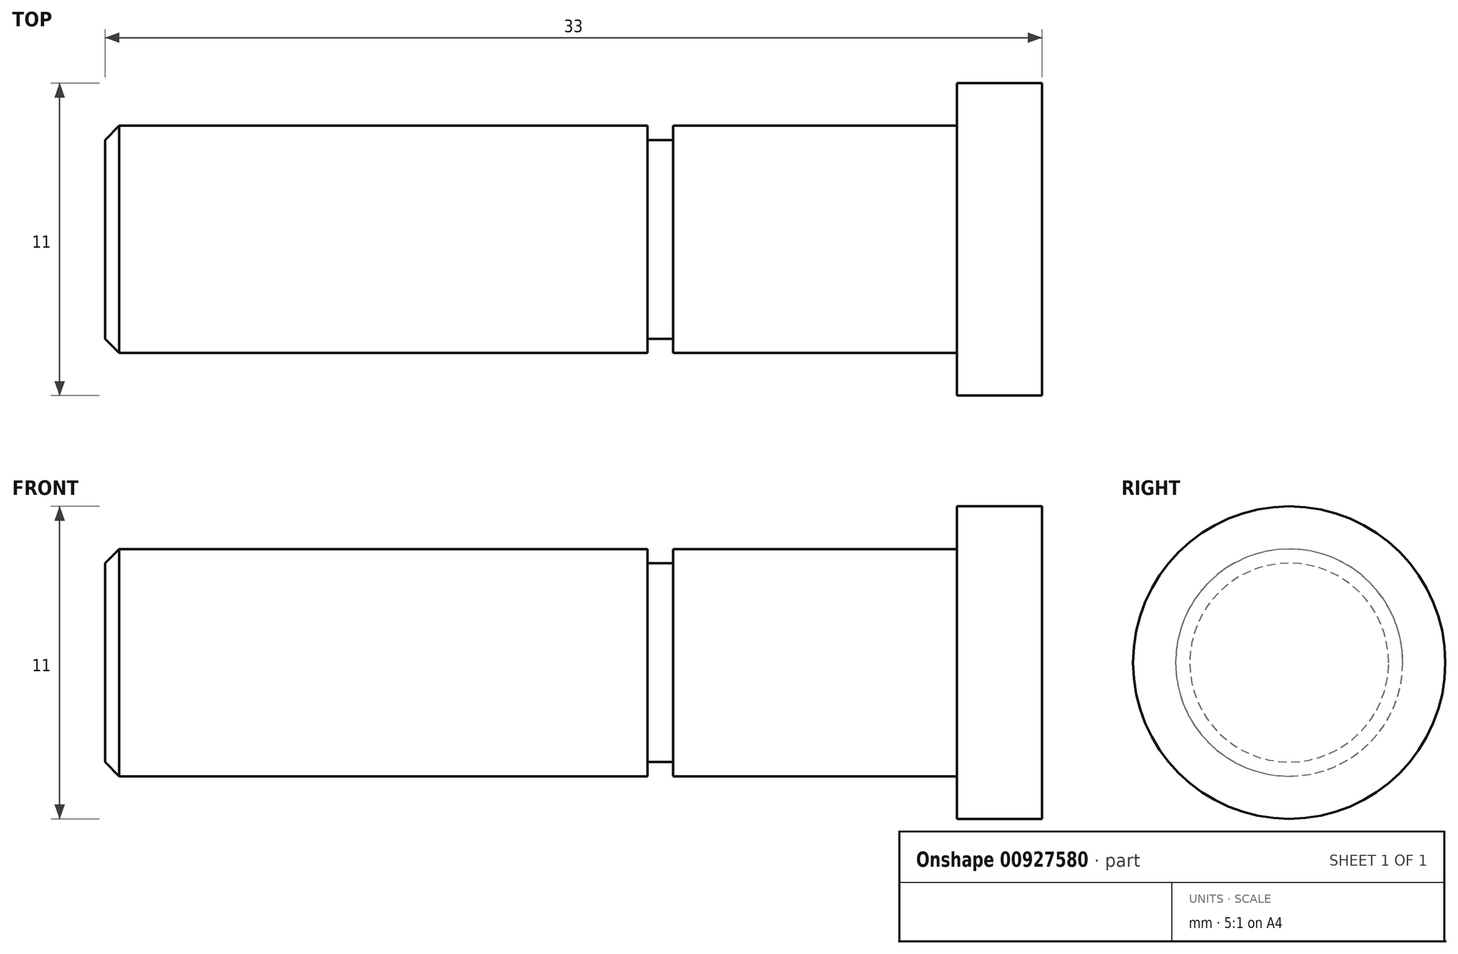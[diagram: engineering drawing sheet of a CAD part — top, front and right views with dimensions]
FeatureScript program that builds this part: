
annotation { "Feature Type Name" : "Feature", "Feature Type Description" : "" }
export const myFeature = defineFeature(function(context is Context, id is Id, definition is map)
    precondition{}
    {
        {
            var Q0;
            Q0=qCreatedBy(makeId("Right.planeOp"),FACE);
            var sketch = newSketch(context, id + "F0", { "sketchPlane" : qUnion([Q0])});
            skCircle(sketch, "E0", {"center": v(0, 0) * mm, "radius": 5.5 * mm});
            skSolve(sketch);
        }
        {
            var Q0;
            Q0 = qSketchRegion(id + "F0", true);
            extrude(context, id + "F1", {"entities" : qUnion([Q0]), "oppositeDirection" : true, "depth" : 3 * mm, "offsetDistance" : 25 * mm});
        }
        {
            var Q0;
            Q0=makeQuery(id+"F1.opExtrude","CAP_FACE",FACE,{"disambiguationData":[OSD([sQuery(id+"F0.wireOp",EDGE,"E0")])],"isStart":false});
            var sketch = newSketch(context, id + "F2", { "sketchPlane" : qUnion([Q0])});
            skCircle(sketch, "E1", {"center": v(0, 0) * mm, "radius": 4 * mm});
            skSolve(sketch);
        }
        {
            var Q0;
            Q0 = qSketchRegion(id + "F2", true);
            extrude(context, id + "F3", {"entities" : qUnion([Q0]), "operationType" : NewBodyOperationType.ADD, "depth" : 30 * mm, "offsetDistance" : 25 * mm});
        }
        {
            var Q0;
            Q0=qCreatedBy(makeId("Front.planeOp"),FACE);
            var sketch = newSketch(context, id + "F4", { "sketchPlane" : qUnion([Q0])});
            skLineSegment(sketch, "E2", {"start": v(-13, 15.33) * mm, "end": v(-13, -6.2) * mm, "construction": true});
            skLineSegment(sketch, "E3", {"start": v(-13, 4) * mm, "end": v(-13, 3.5) * mm});
            skLineSegment(sketch, "E4", {"start": v(-13, 3.5) * mm, "end": v(-13.9, 3.5) * mm});
            skLineSegment(sketch, "E5", {"start": v(-13.9, 3.5) * mm, "end": v(-13.9, 4) * mm});
            skLineSegment(sketch, "E6", {"start": v(-38, 0) * mm, "end": v(5.54, 0) * mm, "construction": true});
            skLineSegment(sketch, "E7", {"start": v(-13.9, 4) * mm, "end": v(-13, 4) * mm});
            skSolve(sketch);
        }
        {
            var Q0;
            Q0 = qSketchRegion(id + "F4", true);
            var Q1;
            Q1=sQuery(id+"F4.wireOp",EDGE,"E6");
            revolve(context, id + "F5", {"operationType" : NewBodyOperationType.REMOVE, "surfaceOperationType" : NewSurfaceOperationType.NEW, "entities" : qUnion([Q0]), "axis" : qUnion([Q1]), "revolveType" : RevolveType.FULL, "oppositeDirection" : true});
        }
        {
            var Q0;
            Q0=makeQuery(id+"F3.opExtrude","CAP_EDGE",EDGE,{"disambiguationData":[OSD([sQuery(id+"F2.wireOp",EDGE,"E1")])],"isStart":false});
            chamfer(context, id + "F6", {"entities" : qUnion([Q0]), "width" : 0.5 * mm, "tangentPropagation" : true});
        }
    });
